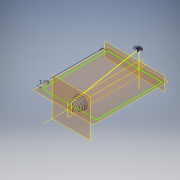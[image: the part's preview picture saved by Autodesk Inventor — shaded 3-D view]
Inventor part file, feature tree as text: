
AUTODESK INVENTOR PART (.ipt)
format: ipt  version: 2018 (Build 220112000, 112)  size: 455,168 bytes
history: native  units: in
note: dims shown in document units (in); Inventor stores cm internally (conversion verified against a paired STEP export)
features: sketch x5, helix x2, plane x1, loft x1, hole x1, other x1, extrude x1, projected_geometry x1
ambient origin geometry x8: Origin, YZ Plane, XZ Plane, XY Plane, X Axis, Y Axis, Z Axis, Center Point
bodies: Solid1 (feature_tree)
feature tree (13):
  sketch  "Sketch1"  dims[d0=2.0in d2=3.9in]
  plane  "Work Plane1"
  loft  "Loft1"
  hole  "Hole1"  [1 undecoded]
  other  "Work Axis2"
  sketch  "Sketch6"  dims[d67=1.0in d68=1.0in d11=0.185in d12=0.75in d13=0.375in d14=0.25in d15=0.5635in d16=1.0in d17=0.8108in d41=0.1in]
  helix  "Coil3"  [1 undecoded]
  helix  "Coil4"  [1 undecoded]
  sketch  "Sketch8"  dims[d42=0.1in d43=0.02in]
  extrude  "Extrusion2"  Depth=0.02in
  sketch  "Sketch2"  dims[d3=0.5in d5=0.0in d6=90.0deg d7=0.0in d8=90.0deg]
  projected_geometry  "Projected Loop1"
  sketch  "Sketch9"  dims[d44=0.13in d45=1.0in d46=11.811in d47=-0.0739in d48=90.0deg d49=90.0deg d50=0.0in d51=0.0in d52=0.13in d53=1.0in d54=11.811in d55=0.0756in d56=90.0deg d57=90.0deg d58=0.0in d59=0.0in d60=3.775in d61=0.02in d62=0.125in d65=0.0in d66=0.5in d69=3.0in d70=0.0in]
note: 3 required parameter values undecoded (feature->parameter linkage not recoverable at this tier; creation-order binding heuristic only, values carry confidence <= 0.55)
